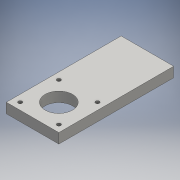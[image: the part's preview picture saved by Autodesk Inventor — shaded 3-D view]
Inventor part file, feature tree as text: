
AUTODESK INVENTOR PART (.ipt)
format: ipt  version: 2016 SP1 (Build 200210100, 210)  size: 104,960 bytes
history: native  units: mm
features: extrude x2, sketch x2, projected_geometry x1
ambient origin geometry x8: Origin, YZ Plane, XZ Plane, XY Plane, X Axis, Y Axis, Z Axis, Center Point
bodies: Solid1 (feature_tree)
feature tree (5):
  extrude  "Extrusion1"  Depth=8.0mm TaperAngle=0.0deg
  extrude  "Extrusion2"  [1 undecoded]
  sketch  "Sketch1"  dims[d0=8.0mm d1=0.0mm d2=50.0mm d3=0.0mm]
  sketch  "Sketch2"
  projected_geometry  "Projected Loop1"
note: 1 required parameter value undecoded (feature->parameter linkage not recoverable at this tier; creation-order binding heuristic only, values carry confidence <= 0.55)
